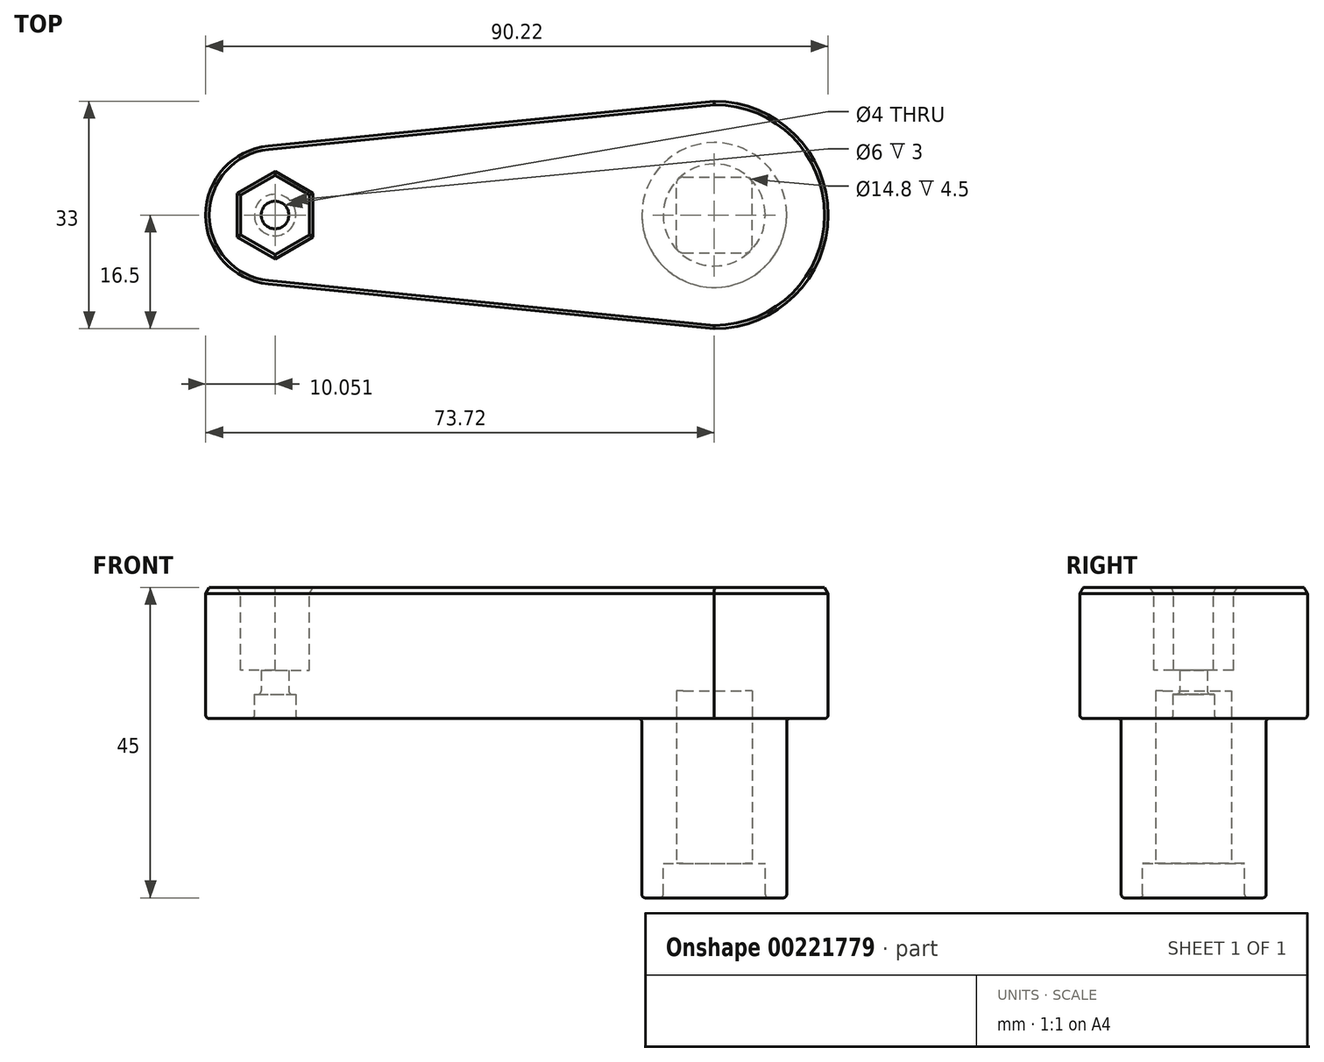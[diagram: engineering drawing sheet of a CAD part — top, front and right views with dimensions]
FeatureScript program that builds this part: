
annotation { "Feature Type Name" : "Feature", "Feature Type Description" : "" }
export const myFeature = defineFeature(function(context is Context, id is Id, definition is map)
    precondition{}
    {
        {
            var Q0;
            Q0=qCreatedBy(makeId("Top.planeOp"),FACE);
            var sketch = newSketch(context, id + "F0", { "sketchPlane" : qUnion([Q0])});
            skCircle(sketch, "E0", {"center": v(0, 0) * mm, "radius": 10.5 * mm});
            skSolve(sketch);
        }
        {
            var Q0;
            Q0 = qSketchRegion(id + "F0", true);
            extrude(context, id + "F1", {"entities" : qUnion([Q0]), "depth" : 40 * mm});
        }
        {
            var Q0;
            Q0=makeQuery(id+"F1.opExtrude","CAP_FACE",FACE,{"disambiguationData":[OSD([sQuery(id+"F0.wireOp",EDGE,"E0")])],"isStart":false});
            var sketch = newSketch(context, id + "F2", { "sketchPlane" : qUnion([Q0])});
            skArc(sketch, "E1", {"start": v(0, -16.5) * mm, "mid": v(16.5, 0) * mm, "end": v(0, 16.5) * mm});
            skCircle(sketch, "E2", {"center": v(0, 0) * mm, "radius": 10.5 * mm});
            skLineSegment(sketch, "E3", {"start": v(0, 16.5) * mm, "end": v(-64.67, 10) * mm});
            skLineSegment(sketch, "E4", {"start": v(0, -16.5) * mm, "end": v(-64.67, -10) * mm});
            skArc(sketch, "E5", {"start": v(-64.67, 10) * mm, "mid": v(-73.72, 0) * mm, "end": v(-64.67, -10) * mm});
            skCircle(sketch, "E6.cCircle", {"center": v(-63.67, 0) * mm, "radius": 5 * mm, "construction": true});
            skLineSegment(sketch, "E6.0", {"start": v(-58.67, 2.89) * mm, "end": v(-58.67, -2.89) * mm});
            skLineSegment(sketch, "E6.1", {"start": v(-58.67, -2.89) * mm, "end": v(-63.67, -5.77) * mm});
            skLineSegment(sketch, "E6.2", {"start": v(-63.67, -5.77) * mm, "end": v(-68.67, -2.89) * mm});
            skLineSegment(sketch, "E6.3", {"start": v(-68.67, -2.89) * mm, "end": v(-68.67, 2.89) * mm});
            skLineSegment(sketch, "E6.4", {"start": v(-68.67, 2.89) * mm, "end": v(-63.67, 5.77) * mm});
            skLineSegment(sketch, "E6.5", {"start": v(-63.67, 5.77) * mm, "end": v(-58.67, 2.89) * mm});
            skPoint(sketch, "E6.0.midPoint", {"position": v(-58.67, 0) * mm});
            skSolve(sketch);
        }
        {
            var Q0;
            Q0 = qSketchRegion(id + "F2", true);
            extrude(context, id + "F3", {"entities" : qUnion([Q0]), "operationType" : NewBodyOperationType.ADD, "oppositeDirection" : true, "depth" : 19 * mm});
        }
        {
            var Q0;
            Q0=makeQuery(id+"F3.opExtrude","CAP_FACE",FACE,{"disambiguationData":[OSD([sQuery(id+"F2.wireOp",EDGE,"E1"),sQuery(id+"F2.wireOp",EDGE,"E2"),sQuery(id+"F2.wireOp",EDGE,"E3"),sQuery(id+"F2.wireOp",EDGE,"E4"),sQuery(id+"F2.wireOp",EDGE,"E5"),sQuery(id+"F2.wireOp",EDGE,"b8vq6PHz-m9iH-EIG8-TIa1-xSA8AQyrFv49"),sQuery(id+"F2.wireOp",EDGE,"Ri83Oy9A-vC9E-eYti-HcYe-lPWJKgM5qgG4"),sQuery(id+"F2.wireOp",EDGE,"JTs3IihE-3t4O-U6pg-v02D-0ebCVmKvNFyC"),sQuery(id+"F2.wireOp",EDGE,"50oUsKVY-NEUj-q7hk-qffv-MLHbQPSXvOP9"),sQuery(id+"F2.wireOp",EDGE,"e622cc0a-1d32-45cb-b124-a9534abca4a2.1.0"),sQuery(id+"F2.wireOp",EDGE,"e622cc0a-1d32-45cb-b124-a9534abca4a2.1.1"),sQuery(id+"F2.wireOp",EDGE,"e622cc0a-1d32-45cb-b124-a9534abca4a2.1.2"),sQuery(id+"F2.wireOp",EDGE,"e622cc0a-1d32-45cb-b124-a9534abca4a2.2.0"),sQuery(id+"F2.wireOp",EDGE,"e622cc0a-1d32-45cb-b124-a9534abca4a2.2.1"),sQuery(id+"F2.wireOp",EDGE,"e622cc0a-1d32-45cb-b124-a9534abca4a2.2.2"),sQuery(id+"F2.wireOp",EDGE,"c88a70be-64de-45f9-8e9c-f09279553d7e.trimOffspring"),sQuery(id+"F2.wireOp",EDGE,"7d05849d-528f-420f-9f3a-91942179a465.trimOffspring")])],"isStart":false});
            var sketch = newSketch(context, id + "F4", { "sketchPlane" : qUnion([Q0])});
            skLineSegment(sketch, "E7", {"start": v(-63.67, 5.77) * mm, "end": v(-58.67, 2.89) * mm});
            skLineSegment(sketch, "E8", {"start": v(-58.67, 2.89) * mm, "end": v(-58.67, -2.89) * mm});
            skLineSegment(sketch, "E9", {"start": v(-58.67, -2.89) * mm, "end": v(-63.67, -5.77) * mm});
            skLineSegment(sketch, "E10", {"start": v(-63.67, -5.77) * mm, "end": v(-68.67, -2.89) * mm});
            skLineSegment(sketch, "E11", {"start": v(-68.67, -2.89) * mm, "end": v(-68.67, 2.89) * mm});
            skLineSegment(sketch, "E12", {"start": v(-68.67, 2.89) * mm, "end": v(-63.67, 5.77) * mm});
            skCircle(sketch, "E13", {"center": v(-63.67, 0) * mm, "radius": 2 * mm});
            skSolve(sketch);
        }
        {
            var Q0;
            Q0 = qSketchRegion(id + "F4", true);
            extrude(context, id + "F5", {"entities" : qUnion([Q0]), "operationType" : NewBodyOperationType.ADD, "oppositeDirection" : true, "depth" : 7 * mm});
        }
        {
            var Q0;
            Q0=makeQuery(id+"F5.boolean.opBoolean","MERGE",FACE,{"derivedFrom":[makeQuery(id+"F3.opExtrude","CAP_FACE",FACE,{"disambiguationData":[OSD([sQuery(id+"F2.wireOp",EDGE,"E1"),sQuery(id+"F2.wireOp",EDGE,"E2"),sQuery(id+"F2.wireOp",EDGE,"E3"),sQuery(id+"F2.wireOp",EDGE,"E4"),sQuery(id+"F2.wireOp",EDGE,"E5"),sQuery(id+"F2.wireOp",EDGE,"b8vq6PHz-m9iH-EIG8-TIa1-xSA8AQyrFv49"),sQuery(id+"F2.wireOp",EDGE,"Ri83Oy9A-vC9E-eYti-HcYe-lPWJKgM5qgG4"),sQuery(id+"F2.wireOp",EDGE,"JTs3IihE-3t4O-U6pg-v02D-0ebCVmKvNFyC"),sQuery(id+"F2.wireOp",EDGE,"50oUsKVY-NEUj-q7hk-qffv-MLHbQPSXvOP9"),sQuery(id+"F2.wireOp",EDGE,"e622cc0a-1d32-45cb-b124-a9534abca4a2.1.0"),sQuery(id+"F2.wireOp",EDGE,"e622cc0a-1d32-45cb-b124-a9534abca4a2.1.1"),sQuery(id+"F2.wireOp",EDGE,"e622cc0a-1d32-45cb-b124-a9534abca4a2.1.2"),sQuery(id+"F2.wireOp",EDGE,"e622cc0a-1d32-45cb-b124-a9534abca4a2.2.0"),sQuery(id+"F2.wireOp",EDGE,"e622cc0a-1d32-45cb-b124-a9534abca4a2.2.1"),sQuery(id+"F2.wireOp",EDGE,"e622cc0a-1d32-45cb-b124-a9534abca4a2.2.2"),sQuery(id+"F2.wireOp",EDGE,"c88a70be-64de-45f9-8e9c-f09279553d7e.trimOffspring"),sQuery(id+"F2.wireOp",EDGE,"7d05849d-528f-420f-9f3a-91942179a465.trimOffspring")])],"isStart":false}),makeQuery(id+"F5.opExtrude","CAP_FACE",FACE,{"disambiguationData":[OSD([sQuery(id+"F4.wireOp",EDGE,"ZtOsYwB5-xBRB-lDCn-l87e-MDY84gHMfsD7"),sQuery(id+"F4.wireOp",EDGE,"sPl1L1Tl-fjGA-x7VE-7h9A-uumigAAZcQGM")])],"isStart":true})]});
            var sketch = newSketch(context, id + "F6", { "sketchPlane" : qUnion([Q0])});
            skCircle(sketch, "E14", {"center": v(-63.67, 0) * mm, "radius": 3 * mm});
            skSolve(sketch);
        }
        {
            var Q0;
            Q0 = qSketchRegion(id + "F6", true);
            extrude(context, id + "F7", {"entities" : qUnion([Q0]), "operationType" : NewBodyOperationType.REMOVE, "oppositeDirection" : true, "depth" : 3.5 * mm});
        }
        {
            var Q0;
            Q0=makeQuery(id+"F1.opExtrude","CAP_FACE",FACE,{"disambiguationData":[OSD([sQuery(id+"F0.wireOp",EDGE,"E0")])],"isStart":true});
            var sketch = newSketch(context, id + "F8", { "sketchPlane" : qUnion([Q0])});
            skLineSegment(sketch, "E15.bottom", {"start": v(-4.5, 5.5) * mm, "end": v(4.5, 5.5) * mm});
            skLineSegment(sketch, "E15.top", {"start": v(-4.5, -5.5) * mm, "end": v(4.5, -5.5) * mm});
            skLineSegment(sketch, "E15.left", {"start": v(-5.5, 4.5) * mm, "end": v(-5.5, -4.5) * mm});
            skLineSegment(sketch, "E15.right", {"start": v(5.5, 4.5) * mm, "end": v(5.5, -4.5) * mm});
            skPoint(sketch, "E15.middle", {"position": v(0, 0) * mm});
            skPoint(sketch, "E16.visualSharp", {"position": v(-5.5, 5.5) * mm});
            skArc(sketch, "E16.filletArc", {"start": v(-4.5, 5.5) * mm, "mid": v(-5.2, 5.2) * mm, "end": v(-5.5, 4.5) * mm});
            skPoint(sketch, "E17.visualSharp", {"position": v(5.5, 5.5) * mm});
            skArc(sketch, "E17.filletArc", {"start": v(5.5, 4.5) * mm, "mid": v(5.2, 5.2) * mm, "end": v(4.5, 5.5) * mm});
            skPoint(sketch, "E18.visualSharp", {"position": v(5.5, -5.5) * mm});
            skArc(sketch, "E18.filletArc", {"start": v(4.5, -5.5) * mm, "mid": v(5.2, -5.2) * mm, "end": v(5.5, -4.5) * mm});
            skPoint(sketch, "E19.visualSharp", {"position": v(-5.5, -5.5) * mm});
            skArc(sketch, "E19.filletArc", {"start": v(-5.5, -4.5) * mm, "mid": v(-5.2, -5.2) * mm, "end": v(-4.5, -5.5) * mm});
            skSolve(sketch);
        }
        {
            var Q0;
            Q0 = qSketchRegion(id + "F8", true);
            extrude(context, id + "F9", {"entities" : qUnion([Q0]), "operationType" : NewBodyOperationType.REMOVE, "oppositeDirection" : true, "depth" : 25 * mm});
        }
        {
            var Q0;
            Q0=makeQuery(id+"F1.opExtrude","CAP_FACE",FACE,{"disambiguationData":[OSD([sQuery(id+"F0.wireOp",EDGE,"E0")])],"isStart":true});
            var sketch = newSketch(context, id + "F10", { "sketchPlane" : qUnion([Q0])});
            skCircle(sketch, "E20", {"center": v(0, 0) * mm, "radius": 10.5 * mm});
            skCircle(sketch, "E21", {"center": v(0, 0) * mm, "radius": 7.4 * mm});
            skSolve(sketch);
        }
        {
            var Q0;
            Q0 = qSketchRegion(id + "F10", true);
            extrude(context, id + "F11", {"entities" : qUnion([Q0]), "operationType" : NewBodyOperationType.ADD, "depth" : 5 * mm});
        }
        {
            var Q0;
            Q0=makeQuery(id+"F5.boolean.opBoolean","MERGE",FACE,{"derivedFrom":[makeQuery(id+"F3.opExtrude","CAP_FACE",FACE,{"disambiguationData":[OSD([sQuery(id+"F2.wireOp",EDGE,"E1"),sQuery(id+"F2.wireOp",EDGE,"E2"),sQuery(id+"F2.wireOp",EDGE,"E3"),sQuery(id+"F2.wireOp",EDGE,"E4"),sQuery(id+"F2.wireOp",EDGE,"E5"),sQuery(id+"F2.wireOp",EDGE,"E6.0"),sQuery(id+"F2.wireOp",EDGE,"E6.1"),sQuery(id+"F2.wireOp",EDGE,"E6.2"),sQuery(id+"F2.wireOp",EDGE,"E6.3"),sQuery(id+"F2.wireOp",EDGE,"E6.4"),sQuery(id+"F2.wireOp",EDGE,"E6.5")])],"isStart":false}),makeQuery(id+"F5.opExtrude","CAP_FACE",FACE,{"disambiguationData":[OSD([sQuery(id+"F4.wireOp",EDGE,"E7"),sQuery(id+"F4.wireOp",EDGE,"E8"),sQuery(id+"F4.wireOp",EDGE,"E9"),sQuery(id+"F4.wireOp",EDGE,"E10"),sQuery(id+"F4.wireOp",EDGE,"E11"),sQuery(id+"F4.wireOp",EDGE,"E12"),sQuery(id+"F4.wireOp",EDGE,"E13")])],"isStart":true})]});
            var Q1;
            Q1=makeQuery(id+"F7.boolean.opBoolean","INTERSECT",EDGE,{"derivedFrom":[makeQuery(id+"F5.opExtrude","SWEPT_FACE",FACE,{"disambiguationData":[OSD([sQuery(id+"F4.wireOp",EDGE,"E13")])]}),makeQuery(id+"F7.opExtrude","CAP_FACE",FACE,{"disambiguationData":[OSD([sQuery(id+"F6.wireOp",EDGE,"E14")])],"isStart":false})]});
            var Q2;
            Q2=makeQuery(id+"F11.opExtrude","CAP_FACE",FACE,{"disambiguationData":[OSD([sQuery(id+"F10.wireOp",EDGE,"E20"),sQuery(id+"F10.wireOp",EDGE,"E21")])],"isStart":false});
            fillet(context, id + "F12", {"entities" : qUnion([Q0, Q1, Q2]), "radius" : .5 * mm, "tangentPropagation" : true, "allowEdgeOverflow" : false});
        }
        {
            var Q0;
            Q0=makeQuery(id+"F3.boolean.opBoolean","MERGE",FACE,{"derivedFrom":[makeQuery(id+"F1.opExtrude","CAP_FACE",FACE,{"disambiguationData":[OSD([sQuery(id+"F0.wireOp",EDGE,"E0")])],"isStart":false}),makeQuery(id+"F3.opExtrude","CAP_FACE",FACE,{"disambiguationData":[OSD([sQuery(id+"F2.wireOp",EDGE,"E1"),sQuery(id+"F2.wireOp",EDGE,"E2"),sQuery(id+"F2.wireOp",EDGE,"E3"),sQuery(id+"F2.wireOp",EDGE,"E4"),sQuery(id+"F2.wireOp",EDGE,"E5"),sQuery(id+"F2.wireOp",EDGE,"E6.0"),sQuery(id+"F2.wireOp",EDGE,"E6.1"),sQuery(id+"F2.wireOp",EDGE,"E6.2"),sQuery(id+"F2.wireOp",EDGE,"E6.3"),sQuery(id+"F2.wireOp",EDGE,"E6.4"),sQuery(id+"F2.wireOp",EDGE,"E6.5")])],"isStart":true})]});
            chamfer(context, id + "F13", {"entities" : qUnion([Q0]), "chamferType" : ChamferType.OFFSET_ANGLE, "width" : .5 * mm, "oppositeDirection" : false, "angle" : 60 * degree, "tangentPropagation" : true});
        }
    });
